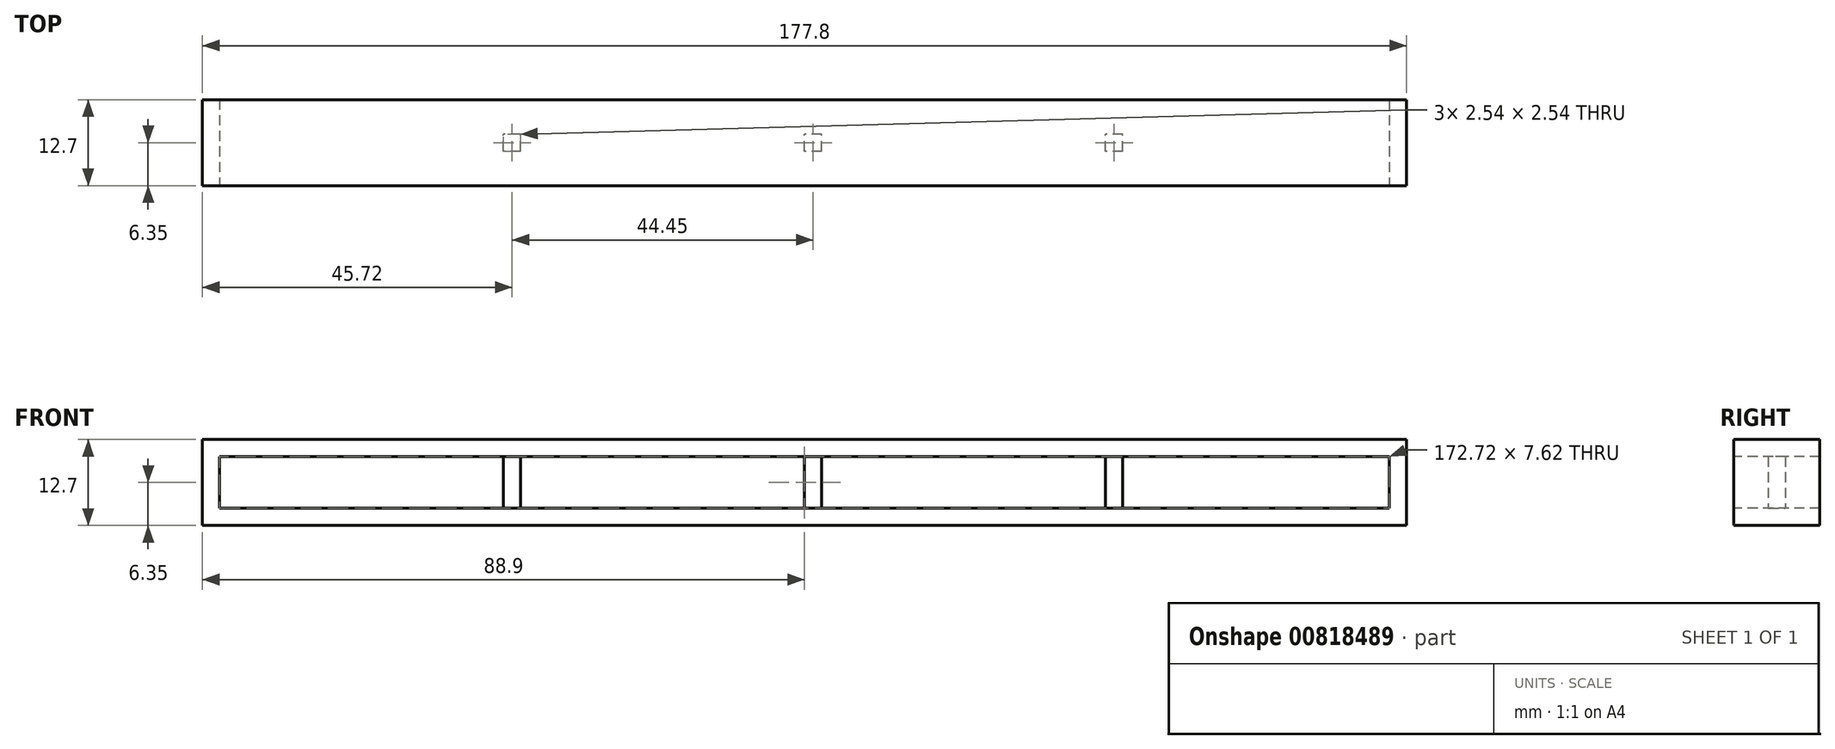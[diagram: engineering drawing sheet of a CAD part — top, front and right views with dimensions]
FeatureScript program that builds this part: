
annotation { "Feature Type Name" : "Feature", "Feature Type Description" : "" }
export const myFeature = defineFeature(function(context is Context, id is Id, definition is map)
    precondition{}
    {
        {
            var Q0;
            Q0=qCreatedBy(makeId("Right.planeOp"),FACE);
            var sketch = newSketch(context, id + "F0", { "sketchPlane" : qUnion([Q0])});
            skLineSegment(sketch, "E0.bottom", {"start": v(0, 0) * mm, "end": v(-12.7, 0) * mm});
            skLineSegment(sketch, "E0.top", {"start": v(0, 2.54) * mm, "end": v(-12.7, 2.54) * mm});
            skLineSegment(sketch, "E0.left", {"start": v(0, 0) * mm, "end": v(0, 2.54) * mm});
            skLineSegment(sketch, "E0.right", {"start": v(-12.7, 0) * mm, "end": v(-12.7, 2.54) * mm});
            skSolve(sketch);
        }
        {
            var Q0;
            Q0=qCreatedBy(makeId("Front.planeOp"),FACE);
            var sketch = newSketch(context, id + "F1", { "sketchPlane" : qUnion([Q0])});
            skLineSegment(sketch, "E1.bottom", {"start": v(0, 0) * mm, "end": v(-177.8, 0) * mm});
            skLineSegment(sketch, "E1.top", {"start": v(0, 12.7) * mm, "end": v(-177.8, 12.7) * mm});
            skLineSegment(sketch, "E1.left", {"start": v(0, 0) * mm, "end": v(0, 12.7) * mm});
            skLineSegment(sketch, "E1.right", {"start": v(-177.8, 0) * mm, "end": v(-177.8, 12.7) * mm});
            skSolve(sketch);
        }
        {
            var Q0;
            Q0=makeQuery(id+"F0.imprint","IMPRINT",FACE,{"disambiguationData":[TD([[makeQuery(id+"F0.imprint","IMPRINT",EDGE,{"derivedFrom":sQuery(id+"F0.wireOp",EDGE,"E0.bottom")}),-1.0]])]});
            var Q1;
            Q1=sQuery(id+"F1.wireOp",EDGE,"E1.left");
            var Q2;
            Q2=sQuery(id+"F1.wireOp",EDGE,"E1.top");
            var Q3;
            Q3=sQuery(id+"F1.wireOp",EDGE,"E1.right");
            var Q4;
            Q4=sQuery(id+"F1.wireOp",EDGE,"E1.bottom");
            sweep(context, id + "F2", {"profiles" : qUnion([Q0]), "path" : qUnion([Q1, Q2, Q3, Q4])});
        }
        {
            var Q0;
            Q0=qCreatedBy(makeId("Top.planeOp"),FACE);
            var sketch = newSketch(context, id + "F3", { "sketchPlane" : qUnion([Q0])});
            skLineSegment(sketch, "E2.bottom", {"start": v(-133.35, -5.08) * mm, "end": v(-130.8, -5.08) * mm});
            skLineSegment(sketch, "E2.top", {"start": v(-133.35, -7.62) * mm, "end": v(-130.8, -7.62) * mm});
            skLineSegment(sketch, "E2.left", {"start": v(-133.35, -5.08) * mm, "end": v(-133.35, -7.62) * mm});
            skLineSegment(sketch, "E2.right", {"start": v(-130.8, -5.08) * mm, "end": v(-130.8, -7.62) * mm});
            skLineSegment(sketch, "E3.1.0.0", {"start": v(-88.9, -5.08) * mm, "end": v(-88.9, -7.62) * mm});
            skLineSegment(sketch, "E3.1.0.1", {"start": v(-88.9, -5.08) * mm, "end": v(-86.36, -5.08) * mm});
            skLineSegment(sketch, "E3.1.0.2", {"start": v(-86.36, -5.08) * mm, "end": v(-86.36, -7.62) * mm});
            skLineSegment(sketch, "E3.1.0.3", {"start": v(-88.9, -7.62) * mm, "end": v(-86.36, -7.62) * mm});
            skLineSegment(sketch, "E3.2.0.0", {"start": v(-44.45, -5.08) * mm, "end": v(-44.45, -7.62) * mm});
            skLineSegment(sketch, "E3.2.0.1", {"start": v(-44.45, -5.08) * mm, "end": v(-41.9, -5.08) * mm});
            skLineSegment(sketch, "E3.2.0.2", {"start": v(-41.9, -5.08) * mm, "end": v(-41.9, -7.62) * mm});
            skLineSegment(sketch, "E3.2.0.3", {"start": v(-44.45, -7.62) * mm, "end": v(-41.9, -7.62) * mm});
            skLineSegment(sketch, "E3.direction1", {"start": v(-133.35, -7.62) * mm, "end": v(-88.9, -7.62) * mm, "construction": true});
            skSolve(sketch);
        }
        {
            var Q0;
            Q0 = qSketchRegion(id + "F3", true);
            extrude(context, id + "F4", {"entities" : qUnion([Q0]), "operationType" : NewBodyOperationType.ADD, "depth" : 12.7 * mm, "offsetDistance" : 25.4 * mm});
        }
    });
